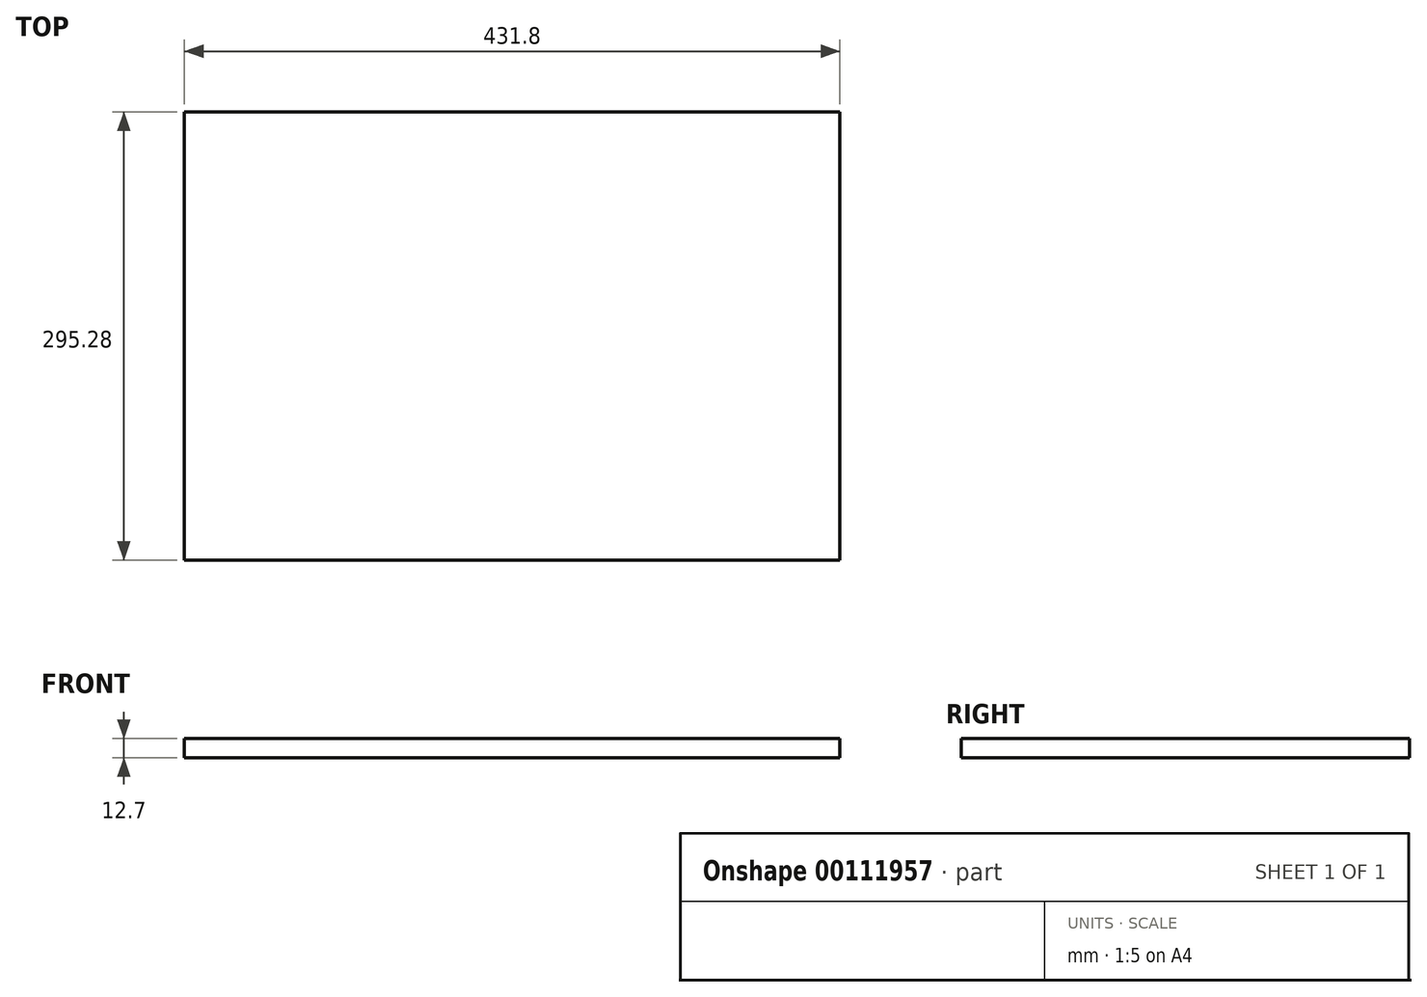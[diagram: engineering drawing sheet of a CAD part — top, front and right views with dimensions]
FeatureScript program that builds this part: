
annotation { "Feature Type Name" : "Feature", "Feature Type Description" : "" }
export const myFeature = defineFeature(function(context is Context, id is Id, definition is map)
    precondition{}
    {
        {
            var Q0;
            Q0=qCreatedBy(makeId("Top.planeOp"),FACE);
            var sketch = newSketch(context, id + "F0", { "sketchPlane" : qUnion([Q0])});
            skLineSegment(sketch, "E0.bottom", {"start": v(-215.9, 147.64) * mm, "end": v(215.9, 147.64) * mm});
            skLineSegment(sketch, "E0.top", {"start": v(-215.9, -147.64) * mm, "end": v(215.9, -147.64) * mm});
            skLineSegment(sketch, "E0.left", {"start": v(-215.9, 147.64) * mm, "end": v(-215.9, -147.64) * mm});
            skLineSegment(sketch, "E0.right", {"start": v(215.9, 147.64) * mm, "end": v(215.9, -147.64) * mm});
            skPoint(sketch, "E0.middle", {"position": v(0, 0) * mm});
            skSolve(sketch);
        }
        {
            var Q0;
            Q0=makeQuery(id+"F0.imprint","IMPRINT",FACE,{"disambiguationData":[TD([[makeQuery(id+"F0.imprint","IMPRINT",EDGE,{"derivedFrom":sQuery(id+"F0.wireOp",EDGE,"E0.bottom")}),-1.0]])]});
            extrude(context, id + "F1", {"entities" : qUnion([Q0]), "depth" : 12.7 * mm});
        }
    });
